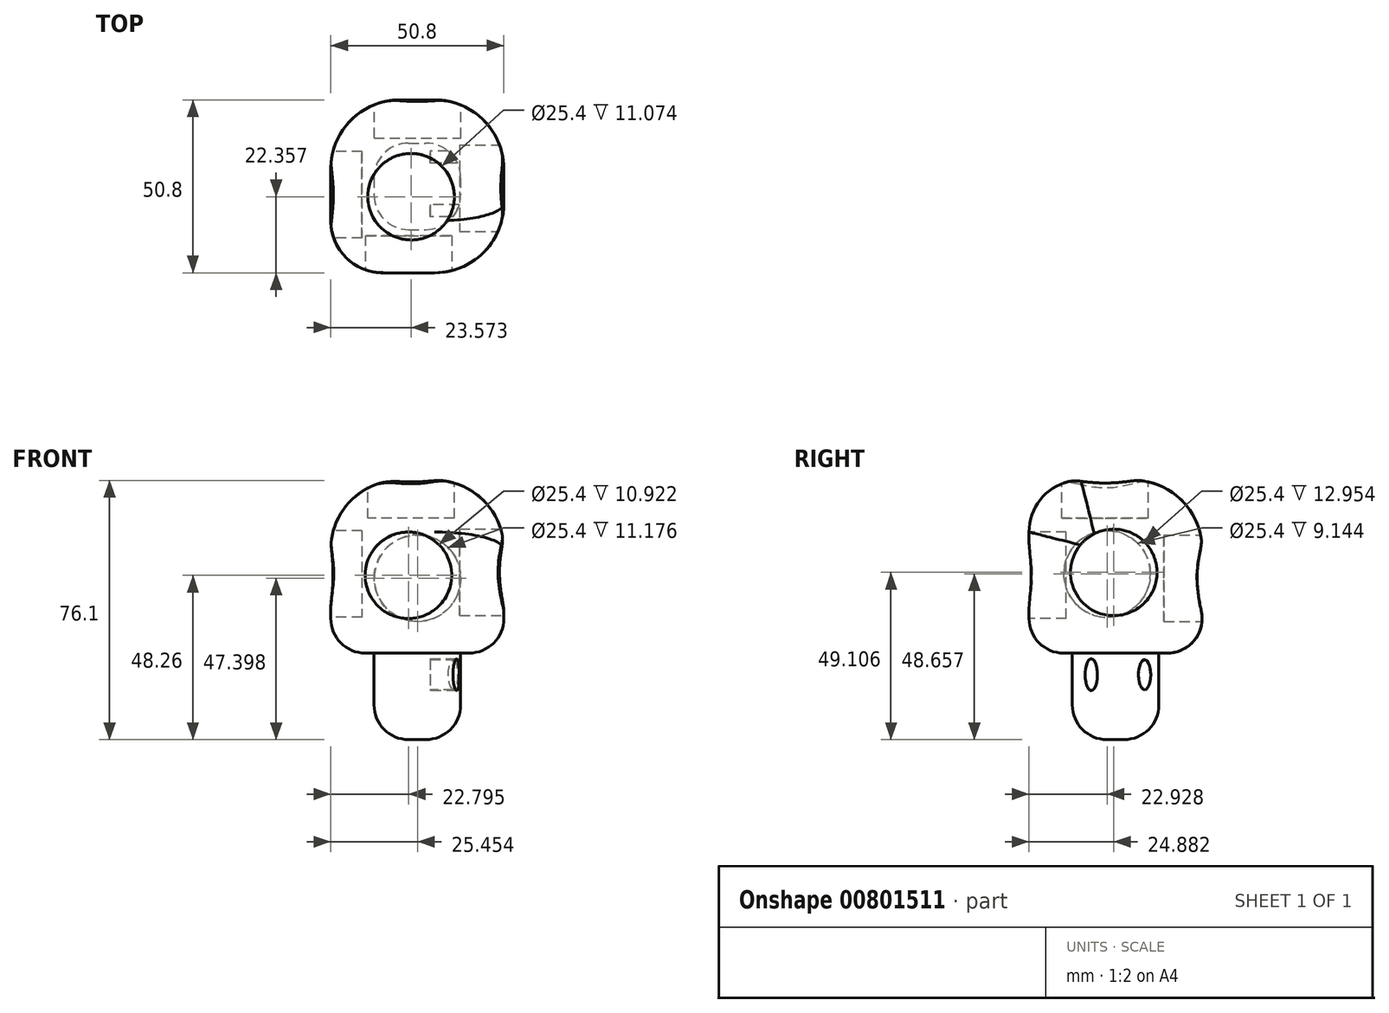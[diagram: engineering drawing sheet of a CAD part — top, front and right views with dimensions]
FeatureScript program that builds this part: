
annotation { "Feature Type Name" : "Feature", "Feature Type Description" : "" }
export const myFeature = defineFeature(function(context is Context, id is Id, definition is map)
    precondition{}
    {
        {
            var Q0;
            Q0=qCreatedBy(makeId("Top.planeOp"),FACE);
            var sketch = newSketch(context, id + "F0", { "sketchPlane" : qUnion([Q0])});
            skLineSegment(sketch, "E0.bottom", {"start": v(-76.62, -36.56) * mm, "end": v(-51.22, -36.56) * mm});
            skLineSegment(sketch, "E0.top", {"start": v(-76.62, -61.96) * mm, "end": v(-51.22, -61.96) * mm});
            skLineSegment(sketch, "E0.left", {"start": v(-76.62, -36.56) * mm, "end": v(-76.62, -61.96) * mm});
            skLineSegment(sketch, "E0.right", {"start": v(-51.22, -36.56) * mm, "end": v(-51.22, -61.96) * mm});
            skSolve(sketch);
        }
        {
            var Q0;
            Q0 = qSketchRegion(id + "F0", true);
            extrude(context, id + "F1", {"entities" : qUnion([Q0]), "depth" : 25.4 * mm, "offsetDistance" : 25.4 * mm});
        }
        {
            var Q0;
            Q0=makeQuery(id+"F1.opExtrude","SWEPT_EDGE",EDGE,{"disambiguationData":[OSD([sQuery(id+"F0.wireOp",EDGE,"E0.bottom"),sQuery(id+"F0.wireOp",EDGE,"E0.left")])]});
            fillet(context, id + "F2", {"entities" : qUnion([Q0]), "radius" : 10.16 * mm, "tangentPropagation" : true, "allowEdgeOverflow" : false});
        }
        {
            var Q0;
            Q0=makeQuery(id+"F1.opExtrude","SWEPT_EDGE",EDGE,{"disambiguationData":[OSD([sQuery(id+"F0.wireOp",EDGE,"E0.top"),sQuery(id+"F0.wireOp",EDGE,"E0.left")])]});
            fillet(context, id + "F3", {"entities" : qUnion([Q0]), "radius" : 10.16 * mm, "tangentPropagation" : true, "allowEdgeOverflow" : false});
        }
        {
            var Q0;
            Q0=makeQuery(id+"F1.opExtrude","SWEPT_EDGE",EDGE,{"disambiguationData":[OSD([sQuery(id+"F0.wireOp",EDGE,"E0.top"),sQuery(id+"F0.wireOp",EDGE,"E0.right")])]});
            fillet(context, id + "F4", {"entities" : qUnion([Q0]), "radius" : 10.16 * mm, "tangentPropagation" : true, "allowEdgeOverflow" : false});
        }
        {
            var Q0;
            Q0=makeQuery(id+"F1.opExtrude","SWEPT_EDGE",EDGE,{"disambiguationData":[OSD([sQuery(id+"F0.wireOp",EDGE,"E0.bottom"),sQuery(id+"F0.wireOp",EDGE,"E0.right")])]});
            fillet(context, id + "F5", {"entities" : qUnion([Q0]), "radius" : 10.16 * mm, "tangentPropagation" : true, "allowEdgeOverflow" : false});
        }
        {
            var Q0;
            Q0=makeQuery(id+"F1.opExtrude","CAP_EDGE",EDGE,{"disambiguationData":[OSD([sQuery(id+"F0.wireOp",EDGE,"E0.left")])],"isStart":true});
            fillet(context, id + "F6", {"entities" : qUnion([Q0]), "radius" : 10.16 * mm, "tangentPropagation" : true, "allowEdgeOverflow" : false});
        }
        {
            var Q0;
            Q0=makeQuery(id+"F1.opExtrude","CAP_FACE",FACE,{"disambiguationData":[OSD([sQuery(id+"F0.wireOp",EDGE,"E0.bottom"),sQuery(id+"F0.wireOp",EDGE,"E0.top"),sQuery(id+"F0.wireOp",EDGE,"E0.left"),sQuery(id+"F0.wireOp",EDGE,"E0.right")])],"isStart":false});
            var sketch = newSketch(context, id + "F7", { "sketchPlane" : qUnion([Q0])});
            skLineSegment(sketch, "E1.bottom", {"start": v(-38.52, -74.66) * mm, "end": v(-89.32, -74.66) * mm});
            skLineSegment(sketch, "E1.top", {"start": v(-38.52, -23.86) * mm, "end": v(-89.32, -23.86) * mm});
            skLineSegment(sketch, "E1.left", {"start": v(-38.52, -74.66) * mm, "end": v(-38.52, -23.86) * mm});
            skLineSegment(sketch, "E1.right", {"start": v(-89.32, -74.66) * mm, "end": v(-89.32, -23.86) * mm});
            skSolve(sketch);
        }
        {
            var Q0;
            Q0 = qSketchRegion(id + "F7", true);
            extrude(context, id + "F8", {"entities" : qUnion([Q0]), "operationType" : NewBodyOperationType.ADD, "depth" : 50.8 * mm, "offsetDistance" : 25.4 * mm});
        }
        {
            var Q0;
            Q0=makeQuery(id+"F8.opExtrude","CAP_EDGE",EDGE,{"disambiguationData":[OSD([sQuery(id+"F7.wireOp",EDGE,"E1.right")])],"isStart":false});
            fillet(context, id + "F9", {"entities" : qUnion([Q0]), "radius" : 20.32 * mm, "tangentPropagation" : true, "allowEdgeOverflow" : false});
        }
        {
            var Q0;
            Q0=makeQuery(id+"F8.opExtrude","CAP_EDGE",EDGE,{"disambiguationData":[OSD([sQuery(id+"F7.wireOp",EDGE,"E1.bottom")])],"isStart":false});
            fillet(context, id + "F10", {"entities" : qUnion([Q0]), "radius" : 15.24 * mm, "tangentPropagation" : true, "allowEdgeOverflow" : false});
        }
        {
            var Q0;
            Q0=makeQuery(id+"F8.opExtrude","CAP_EDGE",EDGE,{"disambiguationData":[OSD([sQuery(id+"F7.wireOp",EDGE,"E1.left")])],"isStart":false});
            fillet(context, id + "F11", {"entities" : qUnion([Q0]), "radius" : 20.32 * mm, "tangentPropagation" : true, "allowEdgeOverflow" : false});
        }
        {
            var Q0;
            Q0=makeQuery(id+"F8.opExtrude","CAP_EDGE",EDGE,{"disambiguationData":[OSD([sQuery(id+"F7.wireOp",EDGE,"E1.top")])],"isStart":false});
            fillet(context, id + "F12", {"entities" : qUnion([Q0]), "radius" : 20.32 * mm, "tangentPropagation" : true, "allowEdgeOverflow" : false});
        }
        {
            var Q0;
            Q0=makeQuery(id+"F8.opExtrude","CAP_EDGE",EDGE,{"disambiguationData":[OSD([sQuery(id+"F7.wireOp",EDGE,"E1.left")])],"isStart":true});
            fillet(context, id + "F13", {"entities" : qUnion([Q0]), "radius" : 10.16 * mm, "tangentPropagation" : true, "allowEdgeOverflow" : false});
        }
        {
            var Q0;
            Q0=makeQuery(id+"F1.opExtrude","SWEPT_FACE",FACE,{"disambiguationData":[OSD([sQuery(id+"F0.wireOp",EDGE,"E0.right")])]});
            var sketch = newSketch(context, id + "F14", { "sketchPlane" : qUnion([Q0])});
            skEllipse(sketch, "E2", {"center": v(-56.38, 19.07) * mm, "majorRadius": 4.71 * mm, "minorRadius": 1.79 * mm, "majorAxis": v(0, 1)});
            skPoint(sketch, "E3.centerSnap0", {"position": v(-54.59, 19.07) * mm});
            skEllipse(sketch, "E4", {"center": v(-40.71, 19.07) * mm, "majorRadius": 4.43 * mm, "minorRadius": 1.8 * mm, "majorAxis": v(0, 1)});
            skSolve(sketch);
        }
        {
            var Q0;
            Q0 = qSketchRegion(id + "F14", true);
            extrude(context, id + "F15", {"entities" : qUnion([Q0]), "operationType" : NewBodyOperationType.REMOVE, "oppositeDirection" : true, "depth" : 8.9 * mm, "offsetDistance" : 25.4 * mm});
        }
        {
            var Q0;
            Q0=makeQuery(id+"F8.opExtrude","SWEPT_FACE",FACE,{"disambiguationData":[OSD([sQuery(id+"F7.wireOp",EDGE,"E1.left")])]});
            var sketch = newSketch(context, id + "F16", { "sketchPlane" : qUnion([Q0])});
            skCircle(sketch, "E5", {"center": v(-49.78, 49.1) * mm, "radius": 12.7 * mm});
            skSolve(sketch);
        }
        {
            var Q0;
            Q0 = qSketchRegion(id + "F16", true);
            extrude(context, id + "F17", {"entities" : qUnion([Q0]), "operationType" : NewBodyOperationType.REMOVE, "oppositeDirection" : true, "depth" : 12.95 * mm, "offsetDistance" : 25.4 * mm});
        }
        {
            var Q0;
            Q0=makeQuery(id+"F8.opExtrude","SWEPT_FACE",FACE,{"disambiguationData":[OSD([sQuery(id+"F7.wireOp",EDGE,"E1.bottom")])]});
            var sketch = newSketch(context, id + "F18", { "sketchPlane" : qUnion([Q0])});
            skCircle(sketch, "E6", {"center": v(-66.53, 48.26) * mm, "radius": 12.7 * mm});
            skPoint(sketch, "E6.centerSnap0", {"position": v(-58.84, 48.26) * mm});
            skSolve(sketch);
        }
        {
            var Q0;
            Q0 = qSketchRegion(id + "F18", true);
            extrude(context, id + "F19", {"entities" : qUnion([Q0]), "operationType" : NewBodyOperationType.REMOVE, "oppositeDirection" : true, "depth" : 10.92 * mm, "offsetDistance" : 25.4 * mm});
        }
        {
            var Q0;
            Q0=makeQuery(id+"F8.opExtrude","SWEPT_FACE",FACE,{"disambiguationData":[OSD([sQuery(id+"F7.wireOp",EDGE,"E1.right")])]});
            var sketch = newSketch(context, id + "F20", { "sketchPlane" : qUnion([Q0])});
            skCircle(sketch, "E7", {"center": v(51.73, 48.66) * mm, "radius": 12.7 * mm});
            skSolve(sketch);
        }
        {
            var Q0;
            Q0 = qSketchRegion(id + "F20", true);
            extrude(context, id + "F21", {"entities" : qUnion([Q0]), "operationType" : NewBodyOperationType.REMOVE, "oppositeDirection" : true, "depth" : 9.14 * mm, "offsetDistance" : 25.4 * mm});
        }
        {
            var Q0;
            Q0=makeQuery(id+"F8.opExtrude","SWEPT_FACE",FACE,{"disambiguationData":[OSD([sQuery(id+"F7.wireOp",EDGE,"E1.top")])]});
            var sketch = newSketch(context, id + "F22", { "sketchPlane" : qUnion([Q0])});
            skCircle(sketch, "E8", {"center": v(63.87, 47.4) * mm, "radius": 12.7 * mm});
            skSolve(sketch);
        }
        {
            var Q0;
            Q0 = qSketchRegion(id + "F22", true);
            extrude(context, id + "F23", {"entities" : qUnion([Q0]), "operationType" : NewBodyOperationType.REMOVE, "oppositeDirection" : true, "depth" : 11.18 * mm, "offsetDistance" : 25.4 * mm});
        }
        {
            var Q0;
            Q0=makeQuery(id+"F8.opExtrude","CAP_FACE",FACE,{"disambiguationData":[OSD([sQuery(id+"F7.wireOp",EDGE,"E1.bottom"),sQuery(id+"F7.wireOp",EDGE,"E1.top"),sQuery(id+"F7.wireOp",EDGE,"E1.left"),sQuery(id+"F7.wireOp",EDGE,"E1.right")])],"isStart":false});
            var sketch = newSketch(context, id + "F24", { "sketchPlane" : qUnion([Q0])});
            skCircle(sketch, "E9", {"center": v(-65.75, -52.3) * mm, "radius": 12.7 * mm});
            skSolve(sketch);
        }
        {
            var Q0;
            Q0 = qSketchRegion(id + "F24", true);
            extrude(context, id + "F25", {"entities" : qUnion([Q0]), "operationType" : NewBodyOperationType.REMOVE, "oppositeDirection" : true, "depth" : 11.18 * mm, "offsetDistance" : 25.4 * mm});
        }
    });
